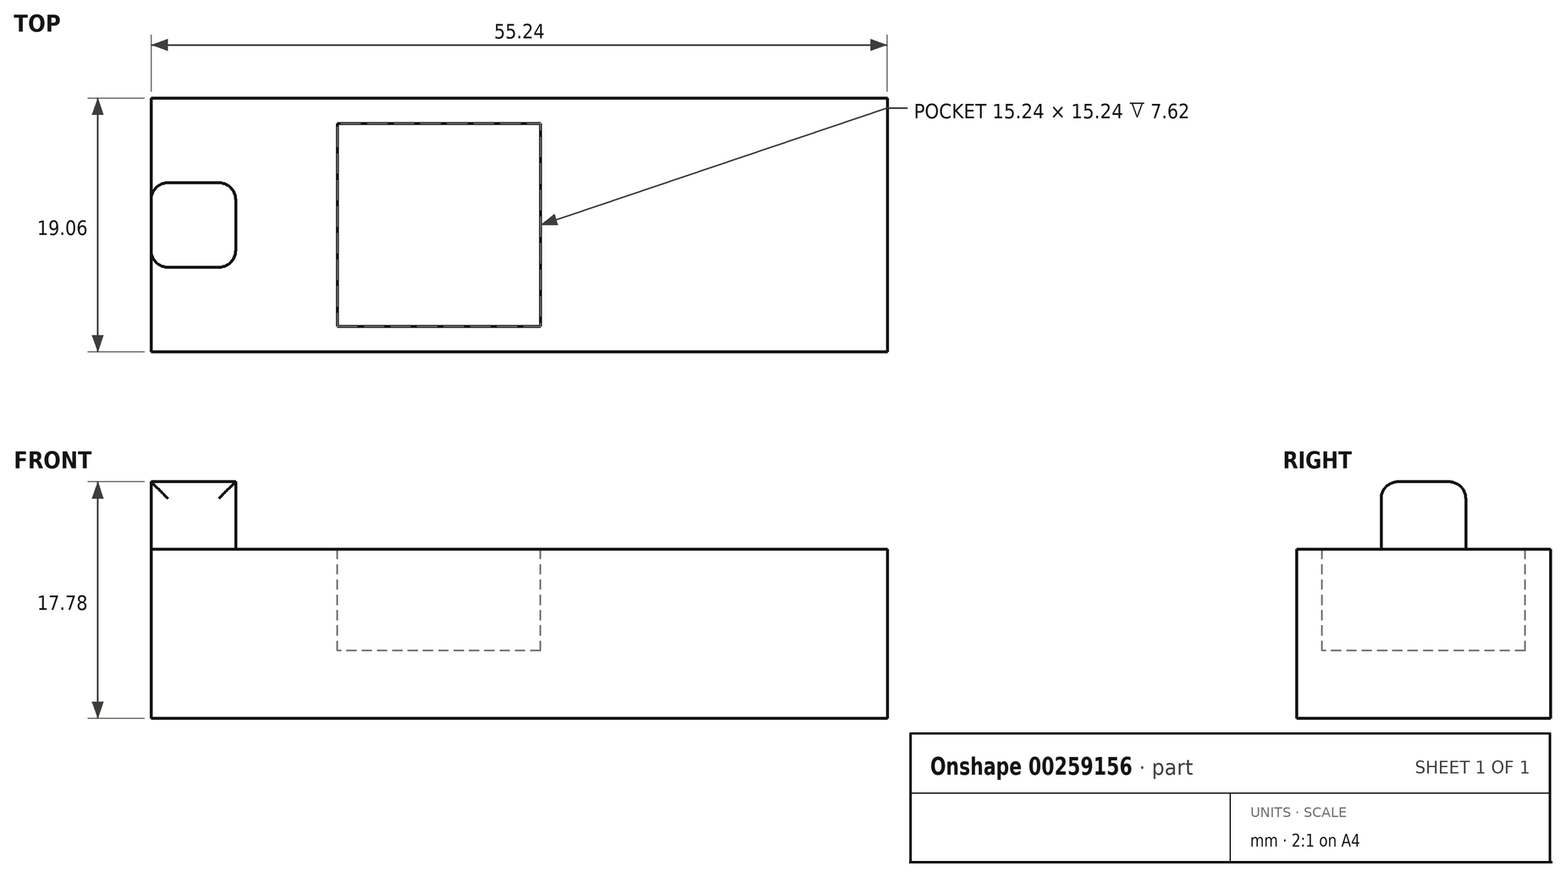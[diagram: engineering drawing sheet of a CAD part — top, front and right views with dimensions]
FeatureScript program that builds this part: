
annotation { "Feature Type Name" : "Feature", "Feature Type Description" : "" }
export const myFeature = defineFeature(function(context is Context, id is Id, definition is map)
    precondition{}
    {
        {
            var Q0;
            Q0=qCreatedBy(makeId("Top.planeOp"),FACE);
            var sketch = newSketch(context, id + "F0", { "sketchPlane" : qUnion([Q0])});
            skLineSegment(sketch, "E0.bottom", {"start": v(23.81, 9.53) * mm, "end": v(-23.81, 9.53) * mm});
            skLineSegment(sketch, "E0.top", {"start": v(23.81, -9.52) * mm, "end": v(-23.81, -9.52) * mm});
            skLineSegment(sketch, "E0.left", {"start": v(23.81, 9.53) * mm, "end": v(23.81, -9.52) * mm});
            skLineSegment(sketch, "E0.right", {"start": v(-23.81, 9.53) * mm, "end": v(-23.81, -9.52) * mm});
            skPoint(sketch, "E0.middle", {"position": v(0, 0) * mm});
            skSolve(sketch);
        }
        {
            var Q0;
            Q0 = qSketchRegion(id + "F0", true);
            var Q1;
            Q1=makeQuery(id+"F0.imprint","IMPRINT",FACE,{"disambiguationData":[TD([[makeQuery(id+"F0.imprint","IMPRINT",EDGE,{"derivedFrom":sQuery(id+"F0.wireOp",EDGE,"E0.bottom")}),1.0]])]});
            extrude(context, id + "F1", {"entities" : qUnion([Q0, Q1]), "depth" : 12.7 * mm});
        }
        {
            var Q0;
            Q0=makeQuery(id+"F1.opExtrude","CAP_FACE",FACE,{"disambiguationData":[OSD([sQuery(id+"F0.wireOp",EDGE,"E0.bottom"),sQuery(id+"F0.wireOp",EDGE,"E0.top"),sQuery(id+"F0.wireOp",EDGE,"E0.left"),sQuery(id+"F0.wireOp",EDGE,"E0.right")])],"isStart":false});
            var sketch = newSketch(context, id + "F2", { "sketchPlane" : qUnion([Q0])});
            skLineSegment(sketch, "E1.bottom", {"start": v(23.81, -9.52) * mm, "end": v(-17.46, -9.52) * mm});
            skLineSegment(sketch, "E1.top", {"start": v(23.81, 9.53) * mm, "end": v(-17.46, 9.53) * mm});
            skLineSegment(sketch, "E1.left", {"start": v(23.81, -9.52) * mm, "end": v(23.81, 9.53) * mm});
            skLineSegment(sketch, "E1.right", {"start": v(-17.46, -9.52) * mm, "end": v(-17.46, 9.53) * mm});
            skLineSegment(sketch, "E2.bottom", {"start": v(-17.46, 9.53) * mm, "end": v(-2.22, 9.53) * mm});
            skLineSegment(sketch, "E2.top", {"start": v(-17.46, -9.52) * mm, "end": v(-2.22, -9.52) * mm});
            skLineSegment(sketch, "E2.left", {"start": v(-17.46, 9.53) * mm, "end": v(-17.46, -9.52) * mm});
            skLineSegment(sketch, "E2.right", {"start": v(-2.22, 9.53) * mm, "end": v(-2.22, -9.52) * mm});
            skLineSegment(sketch, "E3", {"start": v(-2.22, 0) * mm, "end": v(-2.22, 7.62) * mm});
            skLineSegment(sketch, "E4", {"start": v(-2.22, 7.62) * mm, "end": v(-2.22, -7.62) * mm});
            skLineSegment(sketch, "E5.bottom", {"start": v(-2.22, -7.62) * mm, "end": v(-17.46, -7.62) * mm});
            skLineSegment(sketch, "E5.top", {"start": v(-2.22, 7.62) * mm, "end": v(-17.46, 7.62) * mm});
            skLineSegment(sketch, "E5.left", {"start": v(-2.22, -7.62) * mm, "end": v(-2.22, 7.62) * mm});
            skLineSegment(sketch, "E5.right", {"start": v(-17.46, -7.62) * mm, "end": v(-17.46, 7.62) * mm});
            skSolve(sketch);
        }
        {
            var Q0;
            {var subQ4=sQuery(id+"F2.wireOp",EDGE,"E5.bottom");Q0=makeQuery(id+"F2.imprint","IMPRINT",FACE,{"disambiguationData":[TD([[makeQuery(id+"F2.imprint","IMPRINT",EDGE,{"derivedFrom":subQ4}),-1.0]])]});}
            extrude(context, id + "F3", {"entities" : qUnion([Q0]), "operationType" : NewBodyOperationType.REMOVE, "oppositeDirection" : true, "depth" : 7.62 * mm});
        }
        {
            var Q0;
            Q0=makeQuery(id+"F1.opExtrude","SWEPT_FACE",FACE,{"disambiguationData":[OSD([sQuery(id+"F0.wireOp",EDGE,"E0.right")])]});
            var sketch = newSketch(context, id + "F4", { "sketchPlane" : qUnion([Q0])});
            skLineSegment(sketch, "E6.bottom", {"start": v(-9.53, 12.7) * mm, "end": v(9.52, 12.7) * mm});
            skLineSegment(sketch, "E6.top", {"start": v(-9.53, 0) * mm, "end": v(9.52, 0) * mm});
            skLineSegment(sketch, "E6.left", {"start": v(-9.53, 12.7) * mm, "end": v(-9.53, 0) * mm});
            skLineSegment(sketch, "E6.right", {"start": v(9.52, 12.7) * mm, "end": v(9.52, 0) * mm});
            skSolve(sketch);
        }
        {
            var Q0;
            Q0 = qSketchRegion(id + "F4", true);
            extrude(context, id + "F5", {"entities" : qUnion([Q0]), "operationType" : NewBodyOperationType.ADD, "depth" : 7.62 * mm});
        }
        {
            var Q0;
            Q0=makeQuery(id+"F5.boolean.opBoolean","MERGE",FACE,{"derivedFrom":[makeQuery(id+"F1.opExtrude","CAP_FACE",FACE,{"disambiguationData":[OSD([sQuery(id+"F0.wireOp",EDGE,"E0.bottom"),sQuery(id+"F0.wireOp",EDGE,"E0.top"),sQuery(id+"F0.wireOp",EDGE,"E0.left"),sQuery(id+"F0.wireOp",EDGE,"E0.right")])],"isStart":false}),makeQuery(id+"F5.opExtrude","SWEPT_FACE",FACE,{"disambiguationData":[OSD([sQuery(id+"F4.wireOp",EDGE,"E6.bottom")])]})]});
            var sketch = newSketch(context, id + "F6", { "sketchPlane" : qUnion([Q0])});
            skLineSegment(sketch, "E7.bottom", {"start": v(-31.43, 9.53) * mm, "end": v(-25.08, 9.53) * mm});
            skLineSegment(sketch, "E7.top", {"start": v(-31.43, -9.52) * mm, "end": v(-25.08, -9.52) * mm});
            skLineSegment(sketch, "E7.left", {"start": v(-31.43, 9.53) * mm, "end": v(-31.43, -9.52) * mm});
            skLineSegment(sketch, "E7.right", {"start": v(-25.08, 9.53) * mm, "end": v(-25.08, -9.52) * mm});
            skPoint(sketch, "E8.oppositeSnap0", {"position": v(-28.26, 9.53) * mm});
            skPoint(sketch, "E8.oppositeSnap1", {"position": v(-25.08, 0) * mm});
            skLineSegment(sketch, "E8.bottom", {"start": v(-28.26, 9.53) * mm, "end": v(-28.26, 9.53) * mm});
            skLineSegment(sketch, "E8.top", {"start": v(-28.26, 0) * mm, "end": v(-28.26, 0) * mm});
            skLineSegment(sketch, "E8.left", {"start": v(-28.26, 9.53) * mm, "end": v(-28.26, 0) * mm});
            skLineSegment(sketch, "E8.right", {"start": v(-28.26, 9.53) * mm, "end": v(-28.26, 0) * mm});
            skLineSegment(sketch, "E9.bottom", {"start": v(-31.43, 3.18) * mm, "end": v(-25.08, 3.18) * mm});
            skLineSegment(sketch, "E9.top", {"start": v(-31.43, -3.17) * mm, "end": v(-25.08, -3.17) * mm});
            skLineSegment(sketch, "E9.left", {"start": v(-31.43, 3.18) * mm, "end": v(-31.43, -3.17) * mm});
            skLineSegment(sketch, "E9.right", {"start": v(-25.08, 3.18) * mm, "end": v(-25.08, -3.17) * mm});
            skPoint(sketch, "E9.middle", {"position": v(-28.26, 0) * mm});
            skSolve(sketch);
        }
        {
            var Q0;
            Q0=makeQuery(id+"F6.imprint","IMPRINT",FACE,{"disambiguationData":[TD([[makeQuery(id+"F6.imprint","IMPRINT",EDGE,{"derivedFrom":sQuery(id+"F6.wireOp",EDGE,"E9.top")}),1.0]])]});
            extrude(context, id + "F7", {"entities" : qUnion([Q0]), "operationType" : NewBodyOperationType.ADD, "depth" : 5.08 * mm});
        }
        {
            var Q0;
            Q0=makeQuery(id+"F7.opExtrude","CAP_EDGE",EDGE,{"disambiguationData":[OSD([sQuery(id+"F6.wireOp",EDGE,"E9.left")])],"isStart":false});
            var Q1;
            Q1=makeQuery(id+"F7.opExtrude","CAP_EDGE",EDGE,{"disambiguationData":[OSD([sQuery(id+"F6.wireOp",EDGE,"E9.right")])],"isStart":false});
            var Q2;
            Q2=makeQuery(id+"F7.opExtrude","SWEPT_EDGE",EDGE,{"disambiguationData":[OSD([sQuery(id+"F6.wireOp",EDGE,"E7.right"),sQuery(id+"F6.wireOp",EDGE,"E9.top"),sQuery(id+"F6.wireOp",EDGE,"E9.right")])]});
            var Q3;
            Q3=makeQuery(id+"F7.opExtrude","CAP_EDGE",EDGE,{"disambiguationData":[OSD([sQuery(id+"F6.wireOp",EDGE,"E9.top")])],"isStart":false});
            var Q4;
            Q4=makeQuery(id+"F7.opExtrude","CAP_EDGE",EDGE,{"disambiguationData":[OSD([sQuery(id+"F6.wireOp",EDGE,"E9.bottom")])],"isStart":false});
            var Q5;
            Q5=makeQuery(id+"F7.opExtrude","SWEPT_EDGE",EDGE,{"disambiguationData":[OSD([sQuery(id+"F6.wireOp",EDGE,"E7.left"),sQuery(id+"F6.wireOp",EDGE,"E9.top"),sQuery(id+"F6.wireOp",EDGE,"E9.left")])]});
            var Q6;
            Q6=makeQuery(id+"F7.opExtrude","CAP_EDGE",EDGE,{"disambiguationData":[OSD([sQuery(id+"F6.wireOp",EDGE,"E9.top")])],"isStart":true});
            var Q7;
            Q7=makeQuery(id+"F7.opExtrude","CAP_EDGE",EDGE,{"disambiguationData":[OSD([sQuery(id+"F6.wireOp",EDGE,"E9.right")])],"isStart":true});
            var Q8;
            Q8=makeQuery(id+"F7.opExtrude","CAP_EDGE",EDGE,{"disambiguationData":[OSD([sQuery(id+"F6.wireOp",EDGE,"E9.bottom")])],"isStart":true});
            var Q9;
            Q9=makeQuery(id+"F7.opExtrude","SWEPT_EDGE",EDGE,{"disambiguationData":[OSD([sQuery(id+"F6.wireOp",EDGE,"E7.left"),sQuery(id+"F6.wireOp",EDGE,"E9.bottom"),sQuery(id+"F6.wireOp",EDGE,"E9.left")])]});
            var Q10;
            Q10=makeQuery(id+"F7.opExtrude","SWEPT_EDGE",EDGE,{"disambiguationData":[OSD([sQuery(id+"F6.wireOp",EDGE,"E7.right"),sQuery(id+"F6.wireOp",EDGE,"E9.bottom"),sQuery(id+"F6.wireOp",EDGE,"E9.right")])]});
            fillet(context, id + "F8", {"entities" : qUnion([Q0, Q1, Q2, Q3, Q4, Q5, Q6, Q7, Q8, Q9, Q10]), "radius" : 1.27 * mm, "tangentPropagation" : true, "allowEdgeOverflow" : false});
        }
    });
